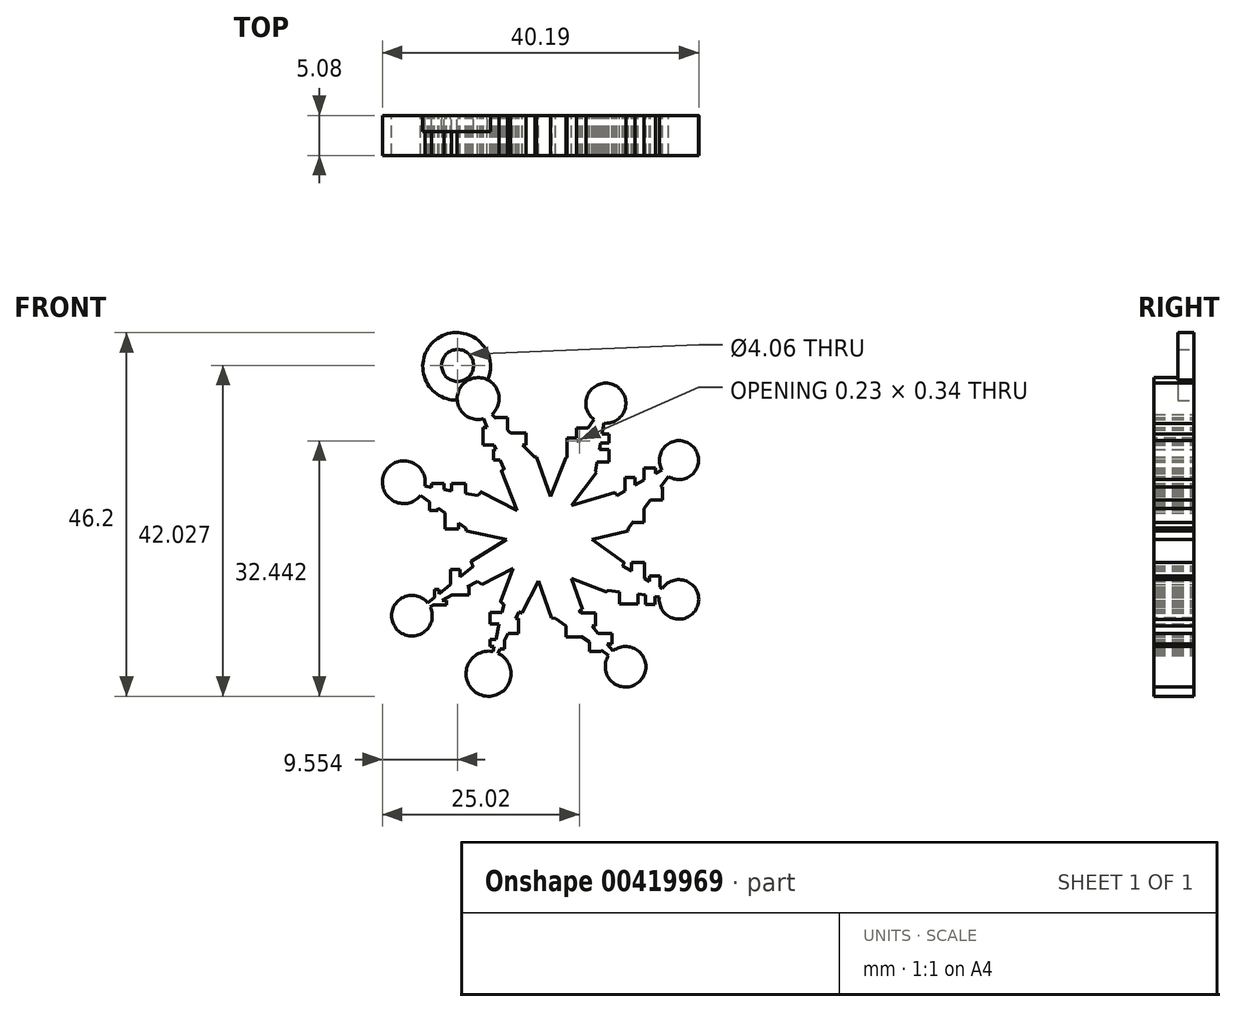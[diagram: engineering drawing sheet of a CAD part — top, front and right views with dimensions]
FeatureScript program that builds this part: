
annotation { "Feature Type Name" : "Feature", "Feature Type Description" : "" }
export const myFeature = defineFeature(function(context is Context, id is Id, definition is map)
    precondition{}
    {
        {
            var Q0;
            Q0=qCreatedBy(makeId("Front.planeOp"),FACE);
            var sketch = newSketch(context, id + "F0", { "sketchPlane" : qUnion([Q0])});
            skCircle(sketch, "E0", {"center": v(0, 0) * mm, "radius": 12.79 * mm});
            skSolve(sketch);
        }
        {
            var Q0;
            Q0=makeQuery(id+"F0.imprint","IMPRINT",FACE,{"disambiguationData":[TD([[makeQuery(id+"F0.imprint","IMPRINT",EDGE,{"derivedFrom":sQuery(id+"F0.wireOp",EDGE,"E0")}),1.0]])]});
            extrude(context, id + "F1", {"entities" : qUnion([Q0]), "depth" : 6.35 * mm});
        }
        {
            var Q0;
            Q0=qCreatedBy(makeId("Front.planeOp"),FACE);
            var sketch = newSketch(context, id + "F2", { "sketchPlane" : qUnion([Q0])});
            skLineSegment(sketch, "E1", {"start": v(-13.03, 1.42) * mm, "end": v(-23.27, 8.7) * mm});
            skLineSegment(sketch, "E2", {"start": v(-23.27, 8.7) * mm, "end": v(-11.17, 6.54) * mm});
            skLineSegment(sketch, "E3", {"start": v(-11.17, 6.54) * mm, "end": v(-6.83, 10.41) * mm});
            skLineSegment(sketch, "E4", {"start": v(-6.83, 10.41) * mm, "end": v(-11.48, 22.04) * mm});
            skLineSegment(sketch, "E5", {"start": v(-11.48, 22.04) * mm, "end": v(-2.03, 12.58) * mm});
            skLineSegment(sketch, "E6", {"start": v(-2.03, 12.58) * mm, "end": v(3.24, 12.58) * mm});
            skLineSegment(sketch, "E7", {"start": v(3.24, 12.58) * mm, "end": v(9.6, 22.04) * mm});
            skLineSegment(sketch, "E8", {"start": v(9.6, 22.04) * mm, "end": v(7.58, 10.41) * mm});
            skLineSegment(sketch, "E9", {"start": v(7.58, 10.41) * mm, "end": v(11, 6.54) * mm});
            skLineSegment(sketch, "E10", {"start": v(11, 6.54) * mm, "end": v(21.54, 12.58) * mm});
            skLineSegment(sketch, "E11", {"start": v(21.54, 12.58) * mm, "end": v(12.85, 1.42) * mm});
            skLineSegment(sketch, "E12", {"start": v(12.85, 1.42) * mm, "end": v(11, -4.16) * mm});
            skLineSegment(sketch, "E13", {"start": v(11, -4.16) * mm, "end": v(21.54, -10.05) * mm});
            skLineSegment(sketch, "E14", {"start": v(21.54, -10.05) * mm, "end": v(9.6, -8.5) * mm});
            skLineSegment(sketch, "E15", {"start": v(9.6, -8.5) * mm, "end": v(4.95, -11.76) * mm});
            skLineSegment(sketch, "E16", {"start": v(4.95, -11.76) * mm, "end": v(12.85, -21.06) * mm});
            skLineSegment(sketch, "E17", {"start": v(12.85, -21.06) * mm, "end": v(1.23, -13) * mm});
            skLineSegment(sketch, "E18", {"start": v(1.23, -13) * mm, "end": v(-4.5, -11.76) * mm});
            skLineSegment(sketch, "E19", {"start": v(-4.5, -11.76) * mm, "end": v(-9.47, -21.68) * mm});
            skLineSegment(sketch, "E20", {"start": v(-9.47, -21.68) * mm, "end": v(-6.83, -10.05) * mm});
            skLineSegment(sketch, "E21", {"start": v(-6.83, -10.05) * mm, "end": v(-11.17, -7.1) * mm});
            skLineSegment(sketch, "E22", {"start": v(-11.17, -7.1) * mm, "end": v(-22.18, -13) * mm});
            skLineSegment(sketch, "E23", {"start": v(-22.18, -13) * mm, "end": v(-11.17, -4.16) * mm});
            skLineSegment(sketch, "E24", {"start": v(-11.17, -4.16) * mm, "end": v(-13.03, 1.42) * mm});
            skSolve(sketch);
        }
        {
            var Q0;
            Q0=makeQuery(id+"F2.imprint","IMPRINT",FACE,{"disambiguationData":[TD([[makeQuery(id+"F2.imprint","IMPRINT",EDGE,{"derivedFrom":sQuery(id+"F2.wireOp",EDGE,"E1")}),-1.0]])]});
            extrude(context, id + "F3", {"entities" : qUnion([Q0]), "operationType" : NewBodyOperationType.ADD, "depth" : 6.35 * mm});
        }
        {
            var Q0;
            Q0=qCreatedBy(makeId("Front.planeOp"),FACE);
            var sketch = newSketch(context, id + "F4", { "sketchPlane" : qUnion([Q0])});
            skCircle(sketch, "E25", {"center": v(-22.86, 8.66) * mm, "radius": 3.4 * mm});
            skCircle(sketch, "E26", {"center": v(-11.06, 21.94) * mm, "radius": 3.32 * mm});
            skCircle(sketch, "E27", {"center": v(9.22, 21.2) * mm, "radius": 3.18 * mm});
            skCircle(sketch, "E28", {"center": v(-21.57, -12.54) * mm, "radius": 3.22 * mm});
            skCircle(sketch, "E29", {"center": v(20.83, 12.17) * mm, "radius": 3.1 * mm});
            skCircle(sketch, "E30", {"center": v(20.83, -9.96) * mm, "radius": 3.14 * mm});
            skCircle(sketch, "E31", {"center": v(12.35, -20.65) * mm, "radius": 3.22 * mm});
            skCircle(sketch, "E32", {"center": v(-9.4, -21.75) * mm, "radius": 3.58 * mm});
            skSolve(sketch);
        }
        {
            var Q0;
            Q0 = qSketchRegion(id + "F4", true);
            extrude(context, id + "F5", {"entities" : qUnion([Q0]), "operationType" : NewBodyOperationType.ADD, "depth" : 6.35 * mm});
        }
        {
            var Q0;
            Q0=qCreatedBy(makeId("Front.planeOp"),FACE);
            var sketch = newSketch(context, id + "F6", { "sketchPlane" : qUnion([Q0])});
            skLineSegment(sketch, "E33", {"start": v(-11.25, 6.45) * mm, "end": v(-5.53, 3.69) * mm});
            skLineSegment(sketch, "E34", {"start": v(-5.53, 3.69) * mm, "end": v(-7.56, 10.14) * mm});
            skLineSegment(sketch, "E35", {"start": v(-7.56, 10.14) * mm, "end": v(-11.25, 6.45) * mm});
            skSolve(sketch);
        }
        {
            var Q0;
            Q0 = qSketchRegion(id + "F6", true);
            extrude(context, id + "F7", {"entities" : qUnion([Q0]), "operationType" : NewBodyOperationType.REMOVE, "endBound" : BoundingType.THROUGH_ALL, "oppositeDirection" : true, "depth" : 25.4 * mm});
        }
        {
            var Q0;
            Q0=qCreatedBy(makeId("Front.planeOp"),FACE);
            var sketch = newSketch(context, id + "F8", { "sketchPlane" : qUnion([Q0])});
            skLineSegment(sketch, "E36", {"start": v(-11.69, 7.7) * mm, "end": v(-4.9, 4.15) * mm});
            skLineSegment(sketch, "E37", {"start": v(-4.9, 4.15) * mm, "end": v(-7.75, 11.39) * mm});
            skLineSegment(sketch, "E38", {"start": v(-7.75, 11.39) * mm, "end": v(-11.69, 7.7) * mm});
            skLineSegment(sketch, "E39", {"start": v(-1.94, 13.2) * mm, "end": v(0.47, 6.4) * mm});
            skLineSegment(sketch, "E40", {"start": v(0.47, 6.4) * mm, "end": v(3.1, 13.2) * mm});
            skLineSegment(sketch, "E41", {"start": v(3.1, 13.2) * mm, "end": v(-1.94, 13.2) * mm});
            skLineSegment(sketch, "E42", {"start": v(8.04, 10.62) * mm, "end": v(3.76, 4.96) * mm});
            skLineSegment(sketch, "E43", {"start": v(3.76, 4.96) * mm, "end": v(11.44, 7.28) * mm});
            skLineSegment(sketch, "E44", {"start": v(11.44, 7.28) * mm, "end": v(8.04, 10.62) * mm});
            skLineSegment(sketch, "E45", {"start": v(13.3, 1.08) * mm, "end": v(7.05, -0.45) * mm});
            skLineSegment(sketch, "E46", {"start": v(7.05, -0.45) * mm, "end": v(12.97, -4.73) * mm});
            skLineSegment(sketch, "E47", {"start": v(12.97, -4.73) * mm, "end": v(13.3, 1.08) * mm});
            skLineSegment(sketch, "E48", {"start": v(5.68, -12.01) * mm, "end": v(3.76, -6.59) * mm});
            skLineSegment(sketch, "E49", {"start": v(3.76, -6.59) * mm, "end": v(10.57, -9.22) * mm});
            skLineSegment(sketch, "E50", {"start": v(10.57, -9.22) * mm, "end": v(5.68, -12.01) * mm});
            skLineSegment(sketch, "E51", {"start": v(-4.3, -12.5) * mm, "end": v(-1.45, -7.06) * mm});
            skLineSegment(sketch, "E52", {"start": v(-1.45, -7.06) * mm, "end": v(0.82, -13.46) * mm});
            skLineSegment(sketch, "E53", {"start": v(0.82, -13.46) * mm, "end": v(-4.3, -12.5) * mm});
            skLineSegment(sketch, "E54", {"start": v(-13.78, 1.08) * mm, "end": v(-6.54, -0.45) * mm});
            skLineSegment(sketch, "E55", {"start": v(-6.54, -0.45) * mm, "end": v(-13.28, -4.56) * mm});
            skLineSegment(sketch, "E56", {"start": v(-13.28, -4.56) * mm, "end": v(-13.78, 1.08) * mm});
            skLineSegment(sketch, "E57", {"start": v(-11.2, -7.96) * mm, "end": v(-5.5, -5.05) * mm});
            skLineSegment(sketch, "E58", {"start": v(-5.5, -5.05) * mm, "end": v(-8.08, -12.01) * mm});
            skLineSegment(sketch, "E59", {"start": v(-8.08, -12.01) * mm, "end": v(-11.2, -7.96) * mm});
            skSolve(sketch);
        }
        {
            var Q0;
            Q0 = qSketchRegion(id + "F8", true);
            extrude(context, id + "F9", {"entities" : qUnion([Q0]), "operationType" : NewBodyOperationType.REMOVE, "endBound" : BoundingType.THROUGH_ALL, "depth" : 25.4 * mm});
        }
        {
            var Q0;
            Q0=qCreatedBy(makeId("Front.planeOp"),FACE);
            var sketch = newSketch(context, id + "F10", { "sketchPlane" : qUnion([Q0])});
            skLineSegment(sketch, "E60.bottom", {"start": v(-16.44, 8.42) * mm, "end": v(-18.47, 8.42) * mm});
            skLineSegment(sketch, "E60.top", {"start": v(-16.44, 7.13) * mm, "end": v(-18.47, 7.13) * mm});
            skLineSegment(sketch, "E60.left", {"start": v(-16.44, 8.42) * mm, "end": v(-16.44, 7.13) * mm});
            skLineSegment(sketch, "E60.right", {"start": v(-18.47, 8.42) * mm, "end": v(-18.47, 7.13) * mm});
            skPoint(sketch, "E60.middle", {"position": v(-17.46, 7.78) * mm});
            skLineSegment(sketch, "E61.bottom", {"start": v(-13.03, 8.42) * mm, "end": v(-15.25, 8.42) * mm});
            skLineSegment(sketch, "E61.top", {"start": v(-13.03, 5.84) * mm, "end": v(-15.25, 5.84) * mm});
            skLineSegment(sketch, "E61.left", {"start": v(-13.03, 8.42) * mm, "end": v(-13.03, 5.84) * mm});
            skLineSegment(sketch, "E61.right", {"start": v(-15.25, 8.42) * mm, "end": v(-15.25, 5.84) * mm});
            skPoint(sketch, "E61.middle", {"position": v(-14.14, 7.13) * mm});
            skLineSegment(sketch, "E62.bottom", {"start": v(-6.4, 18.93) * mm, "end": v(-8.24, 18.93) * mm});
            skLineSegment(sketch, "E62.top", {"start": v(-6.4, 16.9) * mm, "end": v(-8.24, 16.9) * mm});
            skLineSegment(sketch, "E62.left", {"start": v(-6.4, 18.93) * mm, "end": v(-6.4, 16.9) * mm});
            skLineSegment(sketch, "E62.right", {"start": v(-8.24, 18.93) * mm, "end": v(-8.24, 16.9) * mm});
            skPoint(sketch, "E62.middle", {"position": v(-7.32, 17.92) * mm});
            skLineSegment(sketch, "E63.bottom", {"start": v(-3.45, 16.44) * mm, "end": v(-6.21, 16.44) * mm});
            skLineSegment(sketch, "E63.top", {"start": v(-3.45, 14.6) * mm, "end": v(-6.21, 14.6) * mm});
            skLineSegment(sketch, "E63.left", {"start": v(-3.45, 16.44) * mm, "end": v(-3.45, 14.6) * mm});
            skLineSegment(sketch, "E63.right", {"start": v(-6.21, 16.44) * mm, "end": v(-6.21, 14.6) * mm});
            skPoint(sketch, "E63.middle", {"position": v(-4.83, 15.52) * mm});
            skLineSegment(sketch, "E64.bottom", {"start": v(9.73, 14.87) * mm, "end": v(7.15, 14.87) * mm});
            skLineSegment(sketch, "E64.top", {"start": v(9.73, 16.35) * mm, "end": v(7.15, 16.35) * mm});
            skLineSegment(sketch, "E64.left", {"start": v(9.73, 14.87) * mm, "end": v(9.73, 16.35) * mm});
            skLineSegment(sketch, "E64.right", {"start": v(7.15, 14.87) * mm, "end": v(7.15, 16.35) * mm});
            skPoint(sketch, "E64.middle", {"position": v(8.44, 15.61) * mm});
            skLineSegment(sketch, "E65.bottom", {"start": v(18.22, 5.84) * mm, "end": v(16.19, 5.84) * mm});
            skLineSegment(sketch, "E65.top", {"start": v(18.22, 7.87) * mm, "end": v(16.19, 7.87) * mm});
            skLineSegment(sketch, "E65.left", {"start": v(18.22, 5.84) * mm, "end": v(18.22, 7.87) * mm});
            skLineSegment(sketch, "E65.right", {"start": v(16.19, 5.84) * mm, "end": v(16.19, 7.87) * mm});
            skPoint(sketch, "E65.middle", {"position": v(17.2, 6.85) * mm});
            skLineSegment(sketch, "E66.bottom", {"start": v(15.27, 2.25) * mm, "end": v(13.6, 2.25) * mm});
            skLineSegment(sketch, "E66.top", {"start": v(15.27, 4.64) * mm, "end": v(13.6, 4.64) * mm});
            skLineSegment(sketch, "E66.left", {"start": v(15.27, 2.25) * mm, "end": v(15.27, 4.64) * mm});
            skLineSegment(sketch, "E66.right", {"start": v(13.6, 2.25) * mm, "end": v(13.6, 4.64) * mm});
            skPoint(sketch, "E66.middle", {"position": v(14.44, 3.44) * mm});
            skLineSegment(sketch, "E67.bottom", {"start": v(12.22, 9.44) * mm, "end": v(13.88, 9.44) * mm});
            skLineSegment(sketch, "E67.top", {"start": v(12.22, 5.93) * mm, "end": v(13.88, 5.93) * mm});
            skLineSegment(sketch, "E67.left", {"start": v(12.22, 9.44) * mm, "end": v(12.22, 5.93) * mm});
            skLineSegment(sketch, "E67.right", {"start": v(13.88, 9.44) * mm, "end": v(13.88, 5.93) * mm});
            skPoint(sketch, "E67.middle", {"position": v(13.05, 7.68) * mm});
            skLineSegment(sketch, "E68.bottom", {"start": v(15.27, 10.91) * mm, "end": v(17.1, 10.91) * mm});
            skLineSegment(sketch, "E68.top", {"start": v(15.27, 8.51) * mm, "end": v(17.1, 8.51) * mm});
            skLineSegment(sketch, "E68.left", {"start": v(15.27, 10.91) * mm, "end": v(15.27, 8.51) * mm});
            skLineSegment(sketch, "E68.right", {"start": v(17.1, 10.91) * mm, "end": v(17.1, 8.51) * mm});
            skPoint(sketch, "E68.middle", {"position": v(16.19, 9.71) * mm});
            skLineSegment(sketch, "E69.bottom", {"start": v(9.73, 11.83) * mm, "end": v(6.23, 11.83) * mm});
            skLineSegment(sketch, "E69.top", {"start": v(9.73, 13.86) * mm, "end": v(6.23, 13.86) * mm});
            skLineSegment(sketch, "E69.left", {"start": v(9.73, 11.83) * mm, "end": v(9.73, 13.86) * mm});
            skLineSegment(sketch, "E69.right", {"start": v(6.23, 11.83) * mm, "end": v(6.23, 13.86) * mm});
            skPoint(sketch, "E69.middle", {"position": v(7.98, 12.85) * mm});
            skLineSegment(sketch, "E70.bottom", {"start": v(4.57, 17.27) * mm, "end": v(6.6, 17.27) * mm});
            skLineSegment(sketch, "E70.top", {"start": v(4.57, 15.43) * mm, "end": v(6.6, 15.43) * mm});
            skLineSegment(sketch, "E70.left", {"start": v(4.57, 17.27) * mm, "end": v(4.57, 15.43) * mm});
            skLineSegment(sketch, "E70.right", {"start": v(6.6, 17.27) * mm, "end": v(6.6, 15.43) * mm});
            skPoint(sketch, "E70.middle", {"position": v(5.59, 16.35) * mm});
            skLineSegment(sketch, "E71.bottom", {"start": v(-13.95, -5.22) * mm, "end": v(-15.43, -5.22) * mm});
            skLineSegment(sketch, "E71.top", {"start": v(-13.95, -7.99) * mm, "end": v(-15.43, -7.99) * mm});
            skLineSegment(sketch, "E71.left", {"start": v(-13.95, -5.22) * mm, "end": v(-13.95, -7.99) * mm});
            skLineSegment(sketch, "E71.right", {"start": v(-15.43, -5.22) * mm, "end": v(-15.43, -7.99) * mm});
            skPoint(sketch, "E71.middle", {"position": v(-14.7, -6.6) * mm});
            skLineSegment(sketch, "E72.bottom", {"start": v(-17.27, -8.36) * mm, "end": v(-18.01, -8.36) * mm});
            skLineSegment(sketch, "E72.right", {"start": v(-18.01, -8.36) * mm, "end": v(-18.01, -10.57) * mm});
            skLineSegment(sketch, "E73.bottom", {"start": v(-10.27, 14.6) * mm, "end": v(-8.42, 14.6) * mm});
            skLineSegment(sketch, "E73.top", {"start": v(-10.27, 17.36) * mm, "end": v(-8.42, 17.36) * mm});
            skLineSegment(sketch, "E73.left", {"start": v(-10.27, 14.6) * mm, "end": v(-10.27, 17.36) * mm});
            skLineSegment(sketch, "E73.right", {"start": v(-8.42, 14.6) * mm, "end": v(-8.42, 17.36) * mm});
            skPoint(sketch, "E73.middle", {"position": v(-9.35, 15.98) * mm});
            skLineSegment(sketch, "E74.bottom", {"start": v(-8.6, 12.2) * mm, "end": v(-6.76, 12.2) * mm});
            skLineSegment(sketch, "E74.top", {"start": v(-8.6, 13.86) * mm, "end": v(-6.76, 13.86) * mm});
            skLineSegment(sketch, "E74.left", {"start": v(-8.6, 12.2) * mm, "end": v(-8.6, 13.86) * mm});
            skLineSegment(sketch, "E74.right", {"start": v(-6.76, 12.2) * mm, "end": v(-6.76, 13.86) * mm});
            skPoint(sketch, "E74.middle", {"position": v(-7.69, 13.03) * mm});
            skLineSegment(sketch, "E75.bottom", {"start": v(-18.75, 4.18) * mm, "end": v(-17.46, 4.18) * mm});
            skLineSegment(sketch, "E75.top", {"start": v(-18.75, 5.66) * mm, "end": v(-17.46, 5.66) * mm});
            skLineSegment(sketch, "E75.left", {"start": v(-18.75, 4.18) * mm, "end": v(-18.75, 5.66) * mm});
            skLineSegment(sketch, "E75.right", {"start": v(-17.46, 4.18) * mm, "end": v(-17.46, 5.66) * mm});
            skPoint(sketch, "E75.middle", {"position": v(-18.1, 4.92) * mm});
            skLineSegment(sketch, "E76.bottom", {"start": v(-14.14, 1.23) * mm, "end": v(-16.35, 1.23) * mm});
            skLineSegment(sketch, "E76.top", {"start": v(-14.14, 4.18) * mm, "end": v(-16.35, 4.18) * mm});
            skLineSegment(sketch, "E76.left", {"start": v(-14.14, 1.23) * mm, "end": v(-14.14, 4.18) * mm});
            skLineSegment(sketch, "E76.right", {"start": v(-16.35, 1.23) * mm, "end": v(-16.35, 4.18) * mm});
            skPoint(sketch, "E76.middle", {"position": v(-15.25, 2.7) * mm});
            skLineSegment(sketch, "E77.bottom", {"start": v(15.36, -4.11) * mm, "end": v(13.33, -4.11) * mm});
            skLineSegment(sketch, "E77.top", {"start": v(15.36, -7.43) * mm, "end": v(13.33, -7.43) * mm});
            skLineSegment(sketch, "E77.left", {"start": v(15.36, -4.11) * mm, "end": v(15.36, -7.43) * mm});
            skLineSegment(sketch, "E77.right", {"start": v(13.33, -4.11) * mm, "end": v(13.33, -7.43) * mm});
            skPoint(sketch, "E77.middle", {"position": v(14.34, -5.77) * mm});
            skLineSegment(sketch, "E78.bottom", {"start": v(16.19, -6.23) * mm, "end": v(17.85, -6.23) * mm});
            skLineSegment(sketch, "E78.top", {"start": v(16.19, -8.45) * mm, "end": v(17.85, -8.45) * mm});
            skLineSegment(sketch, "E78.left", {"start": v(16.19, -6.23) * mm, "end": v(16.19, -8.45) * mm});
            skLineSegment(sketch, "E78.right", {"start": v(17.85, -6.23) * mm, "end": v(17.85, -8.45) * mm});
            skPoint(sketch, "E78.middle", {"position": v(17.02, -7.34) * mm});
            skLineSegment(sketch, "E79.bottom", {"start": v(14.34, -10.66) * mm, "end": v(11.4, -10.66) * mm});
            skLineSegment(sketch, "E79.top", {"start": v(14.34, -6.79) * mm, "end": v(11.4, -6.79) * mm});
            skLineSegment(sketch, "E79.left", {"start": v(14.34, -10.66) * mm, "end": v(14.34, -6.79) * mm});
            skLineSegment(sketch, "E79.right", {"start": v(11.4, -10.66) * mm, "end": v(11.4, -6.79) * mm});
            skPoint(sketch, "E79.middle", {"position": v(12.87, -8.72) * mm});
            skPoint(sketch, "E79.cornerSnap0", {"position": v(14.34, -7.43) * mm});
            skLineSegment(sketch, "E80.bottom", {"start": v(15.54, -10.75) * mm, "end": v(17.02, -10.75) * mm});
            skLineSegment(sketch, "E80.top", {"start": v(15.54, -8.17) * mm, "end": v(17.02, -8.17) * mm});
            skLineSegment(sketch, "E80.left", {"start": v(15.54, -10.75) * mm, "end": v(15.54, -8.17) * mm});
            skLineSegment(sketch, "E80.right", {"start": v(17.02, -10.75) * mm, "end": v(17.02, -8.17) * mm});
            skPoint(sketch, "E80.middle", {"position": v(16.28, -9.46) * mm});
            skLineSegment(sketch, "E81", {"start": v(-17.27, -8.36) * mm, "end": v(-17.27, -9.83) * mm});
            skLineSegment(sketch, "E82", {"start": v(-17.27, -9.83) * mm, "end": v(-18.01, -10.57) * mm});
            skLineSegment(sketch, "E83.bottom", {"start": v(7.61, -14.16) * mm, "end": v(4.67, -14.16) * mm});
            skLineSegment(sketch, "E83.top", {"start": v(7.61, -12.13) * mm, "end": v(4.67, -12.13) * mm});
            skLineSegment(sketch, "E83.left", {"start": v(7.61, -14.16) * mm, "end": v(7.61, -12.13) * mm});
            skLineSegment(sketch, "E83.right", {"start": v(4.67, -14.16) * mm, "end": v(4.67, -12.13) * mm});
            skPoint(sketch, "E83.middle", {"position": v(6.14, -13.15) * mm});
            skLineSegment(sketch, "E84.bottom", {"start": v(10.2, -17.02) * mm, "end": v(7.8, -17.02) * mm});
            skLineSegment(sketch, "E84.top", {"start": v(10.2, -15.36) * mm, "end": v(7.8, -15.36) * mm});
            skLineSegment(sketch, "E84.left", {"start": v(10.2, -17.02) * mm, "end": v(10.2, -15.36) * mm});
            skLineSegment(sketch, "E84.right", {"start": v(7.8, -17.02) * mm, "end": v(7.8, -15.36) * mm});
            skPoint(sketch, "E84.middle", {"position": v(9, -16.2) * mm});
            skLineSegment(sketch, "E85.bottom", {"start": v(-6.86, -17.85) * mm, "end": v(-7.96, -17.85) * mm});
            skLineSegment(sketch, "E85.top", {"start": v(-6.86, -16.2) * mm, "end": v(-7.96, -16.2) * mm});
            skLineSegment(sketch, "E85.left", {"start": v(-6.86, -17.85) * mm, "end": v(-6.86, -16.2) * mm});
            skLineSegment(sketch, "E85.right", {"start": v(-7.96, -17.85) * mm, "end": v(-7.96, -16.2) * mm});
            skPoint(sketch, "E85.middle", {"position": v(-7.41, -17.02) * mm});
            skLineSegment(sketch, "E86.bottom", {"start": v(-4.64, -15.36) * mm, "end": v(-7.04, -15.36) * mm});
            skLineSegment(sketch, "E86.top", {"start": v(-4.64, -12.96) * mm, "end": v(-7.04, -12.96) * mm});
            skLineSegment(sketch, "E86.left", {"start": v(-4.64, -15.36) * mm, "end": v(-4.64, -12.96) * mm});
            skLineSegment(sketch, "E86.right", {"start": v(-7.04, -15.36) * mm, "end": v(-7.04, -12.96) * mm});
            skPoint(sketch, "E86.middle", {"position": v(-5.84, -14.16) * mm});
            skSolve(sketch);
        }
        {
            var Q0;
            Q0=qCreatedBy(makeId("Front.planeOp"),FACE);
            var sketch = newSketch(context, id + "F11", { "sketchPlane" : qUnion([Q0])});
            skLineSegment(sketch, "E87.bottom", {"start": v(-16.07, -10.84) * mm, "end": v(-18.29, -10.84) * mm});
            skLineSegment(sketch, "E87.top", {"start": v(-16.07, -10.1) * mm, "end": v(-18.29, -10.1) * mm});
            skLineSegment(sketch, "E87.left", {"start": v(-16.07, -10.84) * mm, "end": v(-16.07, -10.1) * mm});
            skLineSegment(sketch, "E87.right", {"start": v(-18.29, -10.84) * mm, "end": v(-18.29, -10.1) * mm});
            skPoint(sketch, "E87.middle", {"position": v(-17.18, -10.48) * mm});
            skLineSegment(sketch, "E88.bottom", {"start": v(-12.48, -9.28) * mm, "end": v(-15.43, -9.28) * mm});
            skLineSegment(sketch, "E88.top", {"start": v(-12.48, -7.99) * mm, "end": v(-15.43, -7.99) * mm});
            skLineSegment(sketch, "E88.left", {"start": v(-12.48, -9.28) * mm, "end": v(-12.48, -7.99) * mm});
            skLineSegment(sketch, "E88.right", {"start": v(-15.43, -9.28) * mm, "end": v(-15.43, -7.99) * mm});
            skPoint(sketch, "E88.middle", {"position": v(-13.95, -8.63) * mm});
            skLineSegment(sketch, "E89.bottom", {"start": v(2.91, -15.91) * mm, "end": v(5.31, -15.91) * mm});
            skLineSegment(sketch, "E89.top", {"start": v(2.91, -13.15) * mm, "end": v(5.31, -13.15) * mm});
            skLineSegment(sketch, "E89.left", {"start": v(2.91, -15.91) * mm, "end": v(2.91, -13.15) * mm});
            skLineSegment(sketch, "E89.right", {"start": v(5.31, -15.91) * mm, "end": v(5.31, -13.15) * mm});
            skPoint(sketch, "E89.middle", {"position": v(4.11, -14.53) * mm});
            skLineSegment(sketch, "E90.bottom", {"start": v(6.6, -18.22) * mm, "end": v(8.44, -18.22) * mm});
            skLineSegment(sketch, "E90.top", {"start": v(6.6, -16.56) * mm, "end": v(8.44, -16.56) * mm});
            skLineSegment(sketch, "E90.left", {"start": v(6.6, -18.22) * mm, "end": v(6.6, -16.56) * mm});
            skLineSegment(sketch, "E90.right", {"start": v(8.44, -18.22) * mm, "end": v(8.44, -16.56) * mm});
            skPoint(sketch, "E90.middle", {"position": v(7.52, -17.39) * mm});
            skLineSegment(sketch, "E91.bottom", {"start": v(-9.16, -13.89) * mm, "end": v(-5.84, -13.89) * mm});
            skLineSegment(sketch, "E91.top", {"start": v(-9.16, -12.04) * mm, "end": v(-5.84, -12.04) * mm});
            skLineSegment(sketch, "E91.left", {"start": v(-9.16, -13.89) * mm, "end": v(-9.16, -12.04) * mm});
            skLineSegment(sketch, "E91.right", {"start": v(-5.84, -13.89) * mm, "end": v(-5.84, -12.04) * mm});
            skPoint(sketch, "E91.middle", {"position": v(-7.5, -12.96) * mm});
            skLineSegment(sketch, "E92.bottom", {"start": v(-9.16, -17.39) * mm, "end": v(-7.87, -17.39) * mm});
            skLineSegment(sketch, "E92.top", {"start": v(-9.16, -16.28) * mm, "end": v(-7.87, -16.28) * mm});
            skLineSegment(sketch, "E92.left", {"start": v(-9.16, -17.39) * mm, "end": v(-9.16, -16.28) * mm});
            skLineSegment(sketch, "E92.right", {"start": v(-7.87, -17.39) * mm, "end": v(-7.87, -16.28) * mm});
            skPoint(sketch, "E92.middle", {"position": v(-8.52, -16.84) * mm});
            skLineSegment(sketch, "E93.bottom", {"start": v(3.04, 15.66) * mm, "end": v(4.87, 15.66) * mm});
            skLineSegment(sketch, "E93.top", {"start": v(3.04, 11.22) * mm, "end": v(4.87, 11.22) * mm});
            skLineSegment(sketch, "E93.left", {"start": v(3.04, 15.66) * mm, "end": v(3.04, 11.22) * mm});
            skLineSegment(sketch, "E93.right", {"start": v(4.87, 15.66) * mm, "end": v(4.87, 11.22) * mm});
            skPoint(sketch, "E93.middle", {"position": v(3.96, 13.44) * mm});
            skSolve(sketch);
        }
        {
            var Q0;
            Q0 = qSketchRegion(id + "F10", true);
            extrude(context, id + "F12", {"entities" : qUnion([Q0]), "operationType" : NewBodyOperationType.ADD, "depth" : 6.35 * mm});
        }
        {
            var Q0;
            Q0 = qSketchRegion(id + "F11", true);
            extrude(context, id + "F13", {"entities" : qUnion([Q0]), "operationType" : NewBodyOperationType.ADD, "depth" : 6.35 * mm});
        }
        {
            var Q0;
            Q0=qCreatedBy(makeId("Front.planeOp"),FACE);
            var sketch = newSketch(context, id + "F14", { "sketchPlane" : qUnion([Q0])});
            skCircle(sketch, "E94", {"center": v(-14.48, 27.04) * mm, "radius": 5.37 * mm});
            skSolve(sketch);
        }
        {
            var Q0;
            Q0=qCreatedBy(makeId("Front.planeOp"),FACE);
            var sketch = newSketch(context, id + "F15", { "sketchPlane" : qUnion([Q0])});
            skCircle(sketch, "E95", {"center": v(-14.32, 27.2) * mm, "radius": 3.14 * mm});
            skSolve(sketch);
        }
        {
            var Q0;
            Q0 = qSketchRegion(id + "F14", true);
            extrude(context, id + "F16", {"entities" : qUnion([Q0]), "operationType" : NewBodyOperationType.ADD, "depth" : 2.54 * mm});
        }
        {
            var Q0;
            Q0=sQuery(id+"F15.wireOp",VERTEX,"E95.center");
            var Q1;
            Q1=makeQuery(id+"F1.opExtrude","SWEPT_BODY",BODY,{"disambiguationData":[OSD([sQuery(id+"F0.wireOp",EDGE,"E0")])]});
            hole(context, id + "F17", {"style" : HoleStyle.SIMPLE, "endStyle" : HoleEndStyle.THROUGH, "oppositeDirection" : true, "holeDiameter" : 5.08 * mm, "isTappedThrough" : true, "tappedDepth" : 12.7 * mm, "tapClearance" : 3, "locations" : qUnion([Q0]), "scope" : qUnion([Q1])});
        }
        {
            var Q0;
            Q0=makeQuery(id+"F1.opExtrude","SWEPT_BODY",BODY,{"disambiguationData":[OSD([sQuery(id+"F0.wireOp",EDGE,"E0")])]});
            var Q1;
            Q1=qCreatedBy(makeId("Origin.pointOp"),VERTEX);
            transform(context, id + "F18", {"entities" : qUnion([Q0]), "transformType" : TransformType.SCALE_UNIFORMLY, "scale" : .8, "scalePoint" : qUnion([Q1]), "makeCopy" : false});
        }
    });
